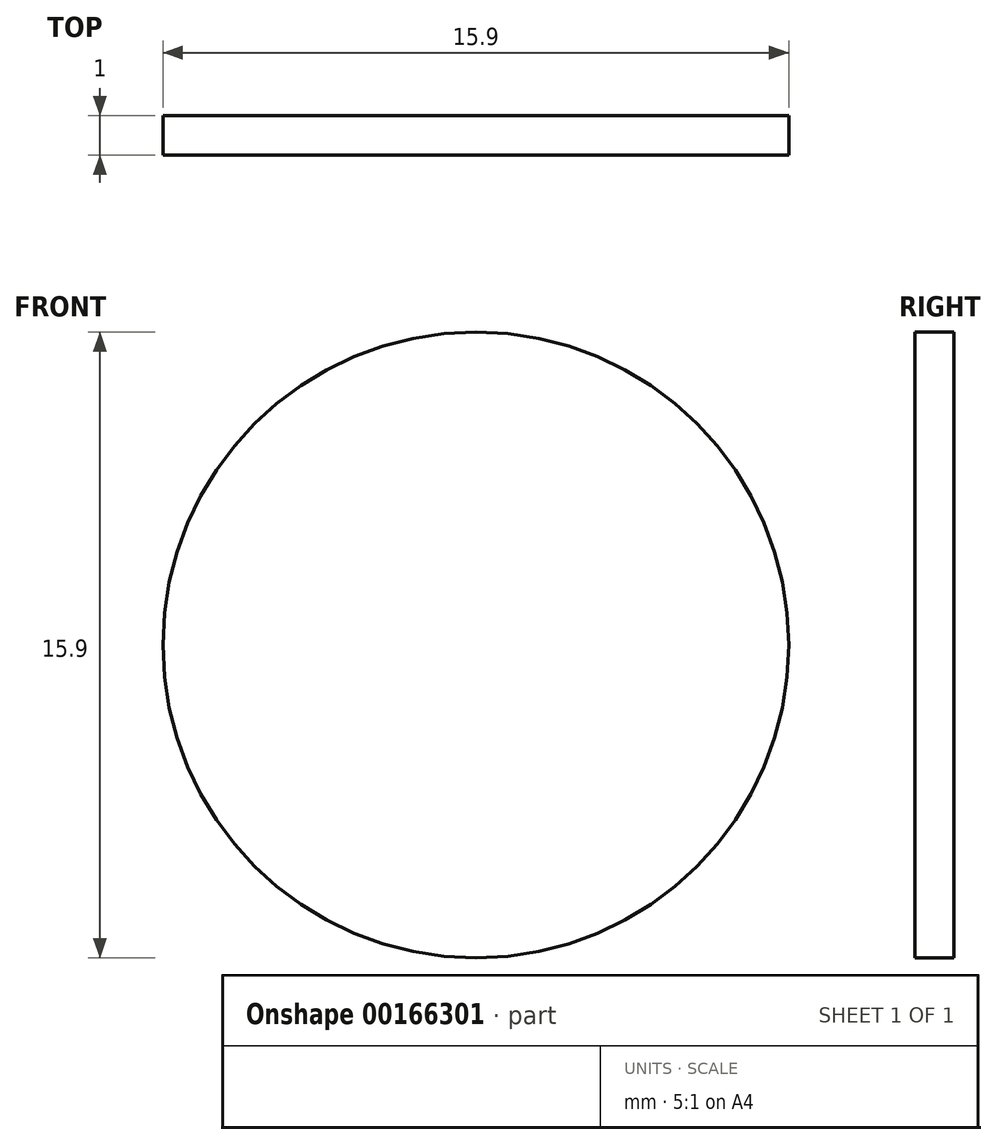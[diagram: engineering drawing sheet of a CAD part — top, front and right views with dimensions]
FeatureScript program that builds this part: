
annotation { "Feature Type Name" : "Feature", "Feature Type Description" : "" }
export const myFeature = defineFeature(function(context is Context, id is Id, definition is map)
    precondition{}
    {
        {
            assignVariable(context, id + "F0", {"name" : "Main_Length", "anyValue" : 1});
        }
        {
            var Q0;
            Q0=qCreatedBy(makeId("Front.planeOp"),FACE);
            var sketch = newSketch(context, id + "F1", { "sketchPlane" : qUnion([Q0])});
            skCircle(sketch, "E0", {"center": v(0, 0) * mm, "radius": 7.95 * mm});
            skSolve(sketch);
        }
        {
            var Q0;
            Q0=makeQuery(id+"F1.imprint","IMPRINT",FACE,{"disambiguationData":[TD([[makeQuery(id+"F1.imprint","IMPRINT",EDGE,{"derivedFrom":sQuery(id+"F1.wireOp",EDGE,"E0")}),1.0]])]});
            extrude(context, id + "F2", {"entities" : qUnion([Q0]), "depth" : (getVariable(context, 'Main_Length')) * mm});
        }
    });
